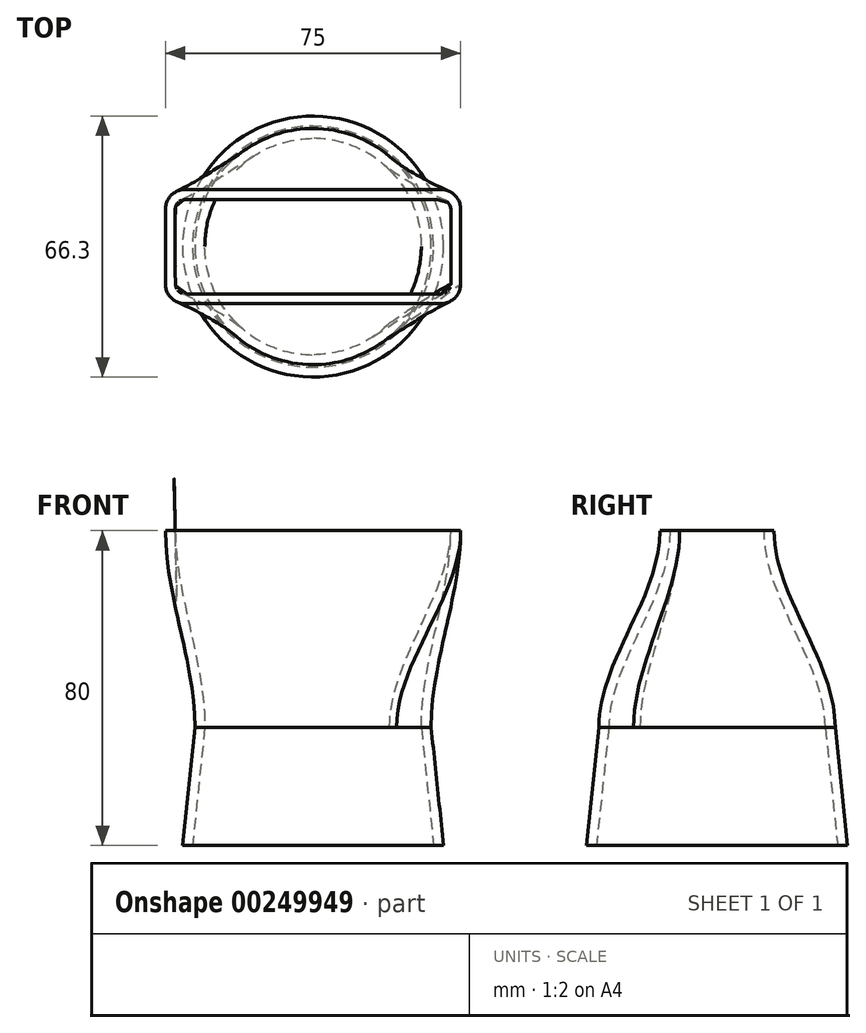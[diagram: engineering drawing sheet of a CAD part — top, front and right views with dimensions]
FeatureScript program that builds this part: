
annotation { "Feature Type Name" : "Feature", "Feature Type Description" : "" }
export const myFeature = defineFeature(function(context is Context, id is Id, definition is map)
    precondition{}
    {
        {
            var Q0;
            Q0=qCreatedBy(makeId("Top.planeOp"),FACE);
            var sketch = newSketch(context, id + "F0", { "sketchPlane" : qUnion([Q0])});
            skCircle(sketch, "E0", {"center": v(0, 0) * mm, "radius": 30 * mm});
            skLineSegment(sketch, "E1", {"start": v(0, 0) * mm, "end": v(0, -30) * mm, "construction": true});
            skLineSegment(sketch, "E2", {"start": v(0, 0) * mm, "end": v(21.21, -21.21) * mm, "construction": true});
            skLineSegment(sketch, "E3", {"start": v(0, 0) * mm, "end": v(21.21, 21.21) * mm, "construction": true});
            skLineSegment(sketch, "E4", {"start": v(0, 0) * mm, "end": v(-21.21, 21.21) * mm, "construction": true});
            skLineSegment(sketch, "E5", {"start": v(0, 0) * mm, "end": v(-21.21, -21.21) * mm, "construction": true});
            skSolve(sketch);
        }
        {
            var Q0;
            Q0=qCreatedBy(makeId("Top.planeOp"),FACE);
            cPlane(context, id + "F1", {"entities" : qUnion([Q0]), "cplaneType" : CPlaneType.OFFSET, "offset" : 50 * mm, "width" : 150 * mm, "height" : 150 * mm});
        }
        {
            var Q0;
            Q0=qCreatedBy(id+"F1.planeOp",FACE);
            var sketch = newSketch(context, id + "F2", { "sketchPlane" : qUnion([Q0])});
            skLineSegment(sketch, "E6.bottom", {"start": v(-32.5, -14.5) * mm, "end": v(32.5, -14.5) * mm});
            skLineSegment(sketch, "E6.top", {"start": v(-32.5, 14.5) * mm, "end": v(32.5, 14.5) * mm});
            skLineSegment(sketch, "E6.left", {"start": v(-37.5, -9.5) * mm, "end": v(-37.5, 9.5) * mm});
            skLineSegment(sketch, "E6.right", {"start": v(37.5, -9.5) * mm, "end": v(37.5, 9.5) * mm});
            skPoint(sketch, "E6.middle", {"position": v(0, 0) * mm});
            skPoint(sketch, "E7.visualSharp", {"position": v(-37.5, -14.5) * mm});
            skArc(sketch, "E7.filletArc", {"start": v(-37.5, -9.5) * mm, "mid": v(-36.04, -13.04) * mm, "end": v(-32.5, -14.5) * mm});
            skPoint(sketch, "E8.visualSharp", {"position": v(-37.5, 14.5) * mm});
            skArc(sketch, "E8.filletArc", {"start": v(-32.5, 14.5) * mm, "mid": v(-36.04, 13.04) * mm, "end": v(-37.5, 9.5) * mm});
            skPoint(sketch, "E9.visualSharp", {"position": v(37.5, 14.5) * mm});
            skArc(sketch, "E9.filletArc", {"start": v(37.5, 9.5) * mm, "mid": v(36.04, 13.04) * mm, "end": v(32.5, 14.5) * mm});
            skPoint(sketch, "E10.visualSharp", {"position": v(37.5, -14.5) * mm});
            skArc(sketch, "E10.filletArc", {"start": v(32.5, -14.5) * mm, "mid": v(36.04, -13.04) * mm, "end": v(37.5, -9.5) * mm});
            skSolve(sketch);
        }
        {
            var Q0;
            Q0=makeQuery(id+"F0.imprint","IMPRINT",FACE,{"disambiguationData":[TD([[makeQuery(id+"F0.imprint","IMPRINT",EDGE,{"derivedFrom":sQuery(id+"F0.wireOp",EDGE,"E0")}),1.0]])]});
            var Q1;
            Q1=makeQuery(id+"F2.imprint","IMPRINT",FACE,{"disambiguationData":[TD([[makeQuery(id+"F2.imprint","IMPRINT",EDGE,{"derivedFrom":sQuery(id+"F2.wireOp",EDGE,"E6.bottom")}),1.0]])]});
            var Q2;
            Q2=sQuery(id+"F2.wireOp",VERTEX,"E6.right.start");
            var Q3;
            Q3=sQuery(id+"F0.wireOp",VERTEX,"E2.end");
            loft(context, id + "F3", {"startCondition" : LoftEndDerivativeType.NORMAL_TO_PROFILE, "startMagnitude" : 1, "endCondition" : LoftEndDerivativeType.NORMAL_TO_PROFILE, "endMagnitude" : 1, "sheetProfilesArray" : [{ "sheetProfileEntities" : qUnion([Q0]) }, { "sheetProfileEntities" : qUnion([Q1]) }], "trimGuidesByProfiles" : true, "matchConnections" : true, "connections" : [{ "connectionEntities" : qUnion([Q2, Q3]), "connectionEdgeQueries" : qUnion([]), "connectionEdgeParameters" : [] }]});
        }
        {
            var Q0;
            Q0=makeQuery(id+"F0.imprint","IMPRINT",FACE,{"disambiguationData":[TD([[makeQuery(id+"F0.imprint","IMPRINT",EDGE,{"derivedFrom":sQuery(id+"F0.wireOp",EDGE,"E0")}),1.0]])]});
            extrude(context, id + "F4", {"entities" : qUnion([Q0]), "operationType" : NewBodyOperationType.ADD, "oppositeDirection" : true, "depth" : 30 * mm, "hasDraft" : true, "draftAngle" : 6 * degree});
        }
        {
            var Q0;
            Q0=makeQuery(id+"F3.opLoft","CAP_FACE",FACE,{"disambiguationData":[OSD([makeQuery(id+"F2.imprint","IMPRINT",FACE,{"disambiguationData":[TD([[makeQuery(id+"F2.imprint","IMPRINT",EDGE,{"derivedFrom":sQuery(id+"F2.wireOp",EDGE,"E6.bottom")}),1.0]])]})])],"isStart":true});
            var Q1;
            Q1=makeQuery(id+"F4.opExtrude","CAP_FACE",FACE,{"disambiguationData":[OSD([sQuery(id+"F0.wireOp",EDGE,"E0")])],"isStart":false});
            shell(context, id + "F5", {"entities" : qUnion([Q0, Q1]), "thickness" : 2.5 * mm});
        }
    });
